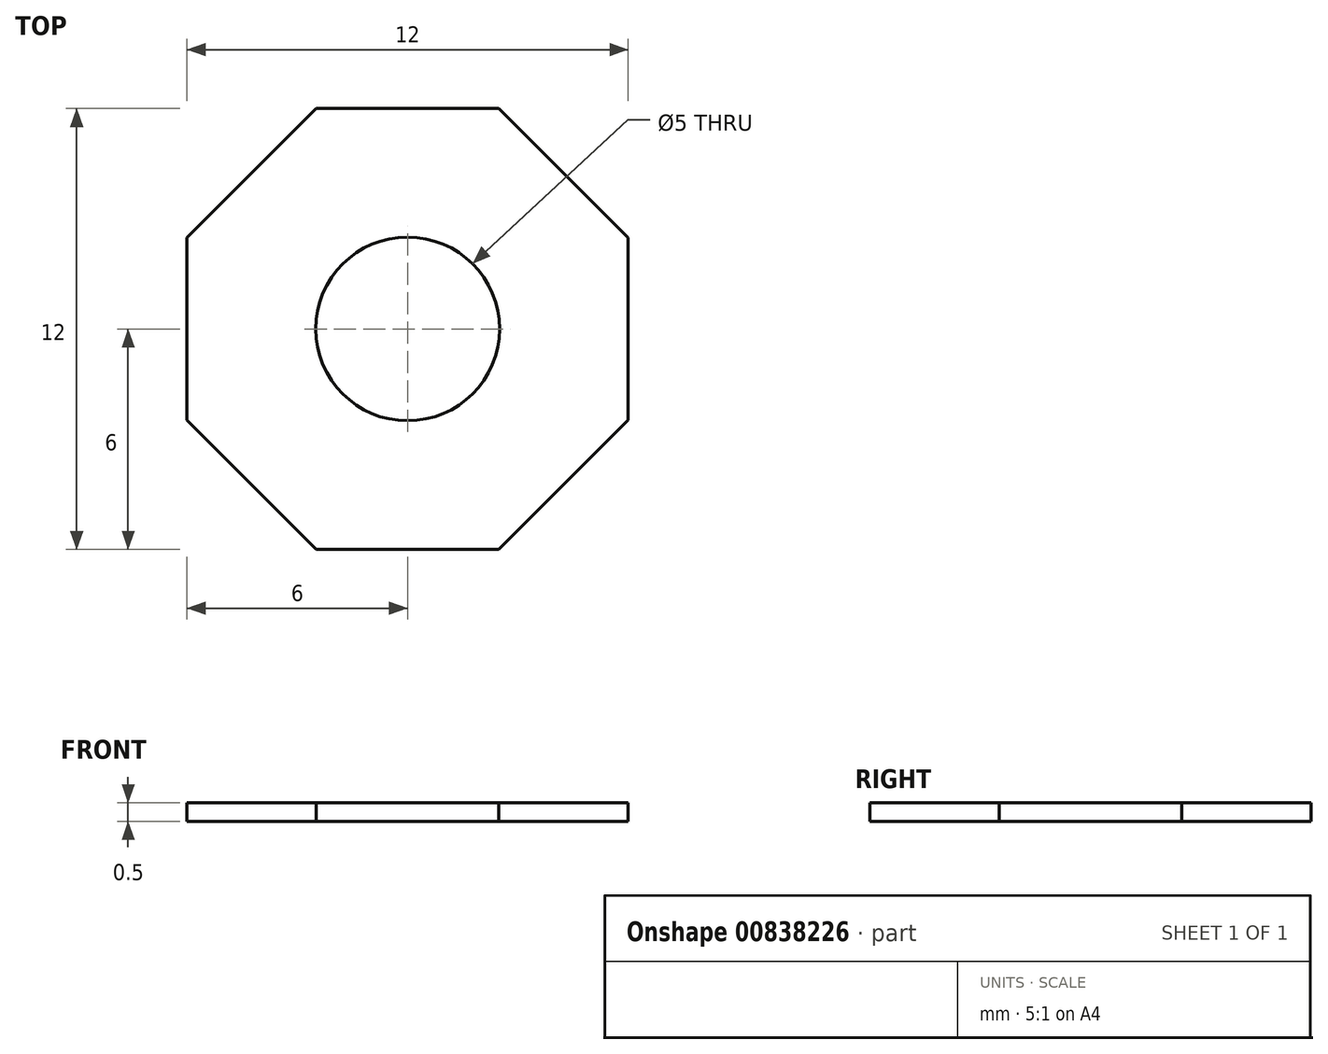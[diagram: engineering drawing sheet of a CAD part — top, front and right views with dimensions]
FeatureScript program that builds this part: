
annotation { "Feature Type Name" : "Feature", "Feature Type Description" : "" }
export const myFeature = defineFeature(function(context is Context, id is Id, definition is map)
    precondition{}
    {
        {
            var Q0;
            Q0=qCreatedBy(makeId("Top.planeOp"),FACE);
            var sketch = newSketch(context, id + "F0", { "sketchPlane" : qUnion([Q0])});
            skCircle(sketch, "E0.cCircle", {"center": v(0, 0) * mm, "radius": 6 * mm, "construction": true});
            skLineSegment(sketch, "E0.0", {"start": v(-2.49, 6) * mm, "end": v(2.49, 6) * mm});
            skLineSegment(sketch, "E0.1", {"start": v(2.49, 6) * mm, "end": v(6, 2.49) * mm});
            skLineSegment(sketch, "E0.2", {"start": v(6, 2.49) * mm, "end": v(6, -2.49) * mm});
            skLineSegment(sketch, "E0.3", {"start": v(6, -2.49) * mm, "end": v(2.49, -6) * mm});
            skLineSegment(sketch, "E0.4", {"start": v(2.49, -6) * mm, "end": v(-2.49, -6) * mm});
            skLineSegment(sketch, "E0.5", {"start": v(-2.49, -6) * mm, "end": v(-6, -2.49) * mm});
            skLineSegment(sketch, "E0.6", {"start": v(-6, -2.49) * mm, "end": v(-6, 2.49) * mm});
            skLineSegment(sketch, "E0.7", {"start": v(-6, 2.49) * mm, "end": v(-2.49, 6) * mm});
            skPoint(sketch, "E0.0.midPoint", {"position": v(0, 6) * mm});
            skCircle(sketch, "E1", {"center": v(0, 0) * mm, "radius": 2.5 * mm});
            skSolve(sketch);
        }
        {
            var Q0;
            Q0=qSketchRegion(id+"F0",true);
            extrude(context, id + "F1", {"entities" : qUnion([Q0]), "depth" : 0.5 * mm, "offsetDistance" : 25 * mm});
        }
    });
